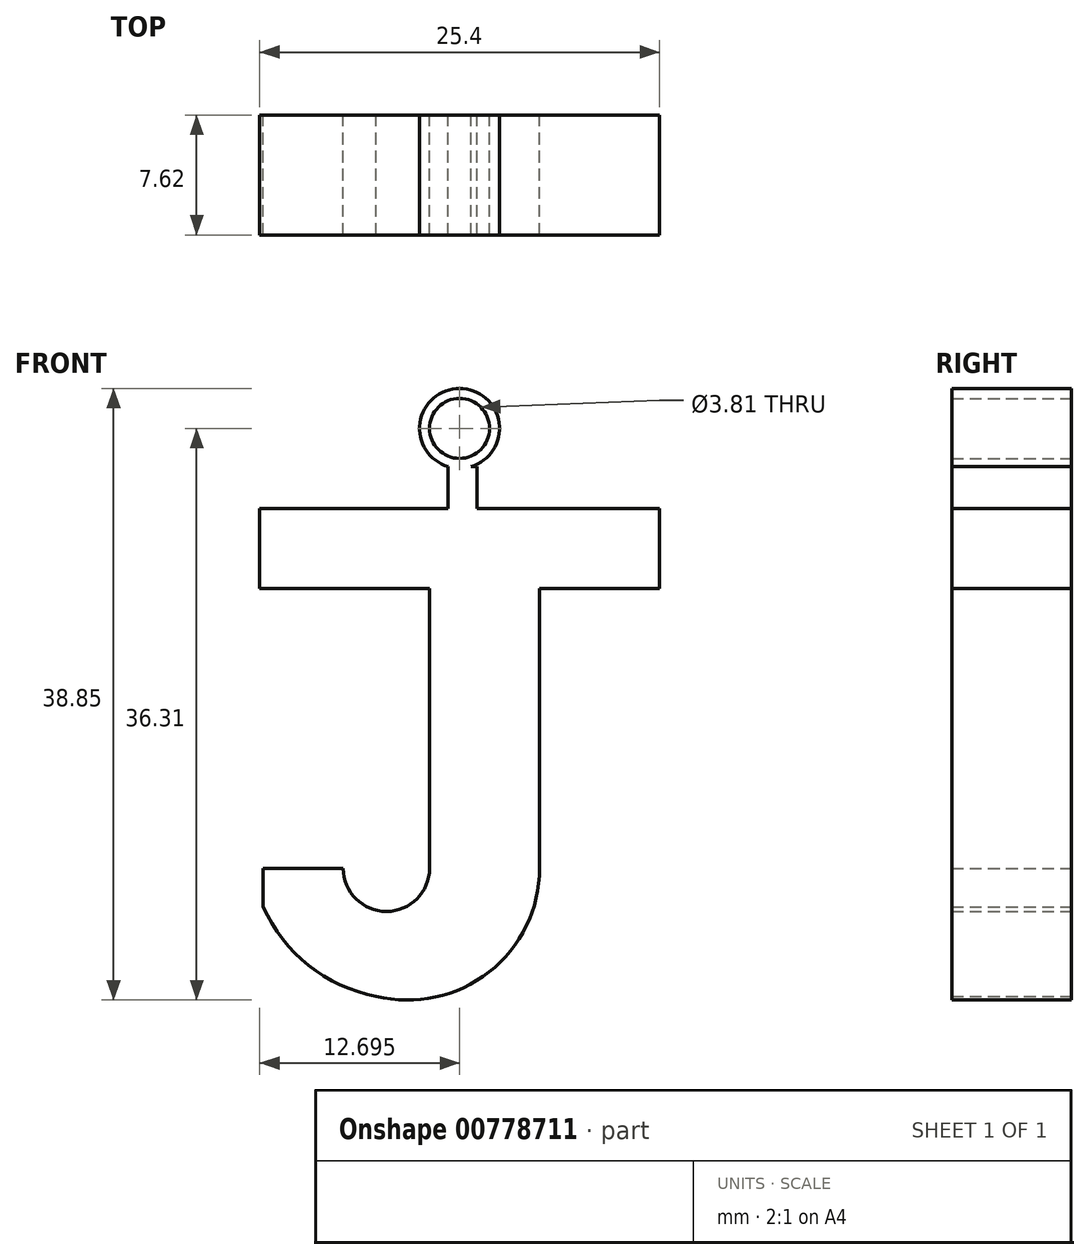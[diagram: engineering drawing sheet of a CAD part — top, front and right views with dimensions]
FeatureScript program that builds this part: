
annotation { "Feature Type Name" : "Feature", "Feature Type Description" : "" }
export const myFeature = defineFeature(function(context is Context, id is Id, definition is map)
    precondition{}
    {
        {
            var Q0;
            Q0=qCreatedBy(makeId("Front.planeOp"),FACE);
            var sketch = newSketch(context, id + "F0", { "sketchPlane" : qUnion([Q0])});
            skLineSegment(sketch, "E0", {"start": v(-10.8, 5.08) * mm, "end": v(14.6, 5.08) * mm});
            skLineSegment(sketch, "E1", {"start": v(14.6, 5.08) * mm, "end": v(14.6, 0) * mm});
            skLineSegment(sketch, "E2", {"start": v(-10.8, 5.08) * mm, "end": v(-10.8, 0) * mm});
            skLineSegment(sketch, "E3", {"start": v(-10.8, 0) * mm, "end": v(0, 0) * mm});
            skLineSegment(sketch, "E4", {"start": v(14.6, 0) * mm, "end": v(6.99, 0) * mm});
            skLineSegment(sketch, "E5", {"start": v(6.99, 0) * mm, "end": v(6.99, -17.78) * mm});
            skArc(sketch, "E6", {"start": v(-3.4, -25.9) * mm, "mid": v(3.77, -24.37) * mm, "end": v(6.99, -17.78) * mm});
            skArc(sketch, "E7", {"start": v(-10.56, -20.22) * mm, "mid": v(-7.69, -23.96) * mm, "end": v(-3.4, -25.9) * mm});
            skLineSegment(sketch, "E8", {"start": v(-10.56, -20.22) * mm, "end": v(-10.56, -17.78) * mm});
            skLineSegment(sketch, "E9", {"start": v(0, -17.78) * mm, "end": v(0, 0) * mm});
            skArc(sketch, "E10", {"start": v(-5.48, -17.78) * mm, "mid": v(-2.74, -20.52) * mm, "end": v(0, -17.78) * mm});
            skLineSegment(sketch, "E11", {"start": v(-5.48, -17.78) * mm, "end": v(-10.56, -17.78) * mm});
            skCircle(sketch, "E12", {"center": v(1.9, 10.16) * mm, "radius": 2.54 * mm});
            skCircle(sketch, "E13", {"center": v(1.9, 10.16) * mm, "radius": 1.9 * mm});
            skLineSegment(sketch, "E14.bottom", {"start": v(1.18, 7.72) * mm, "end": v(3, 7.72) * mm});
            skLineSegment(sketch, "E14.top", {"start": v(1.18, 5.08) * mm, "end": v(3, 5.08) * mm});
            skLineSegment(sketch, "E14.left", {"start": v(1.18, 7.72) * mm, "end": v(1.18, 5.08) * mm});
            skLineSegment(sketch, "E14.right", {"start": v(3, 7.72) * mm, "end": v(3, 5.08) * mm});
            skSolve(sketch);
        }
        {
            var Q0;
            Q0 = qSketchRegion(id + "F0", true);
            extrude(context, id + "F1", {"entities" : qUnion([Q0]), "depth" : 7.62 * mm, "offsetDistance" : 25.4 * mm});
        }
    });
